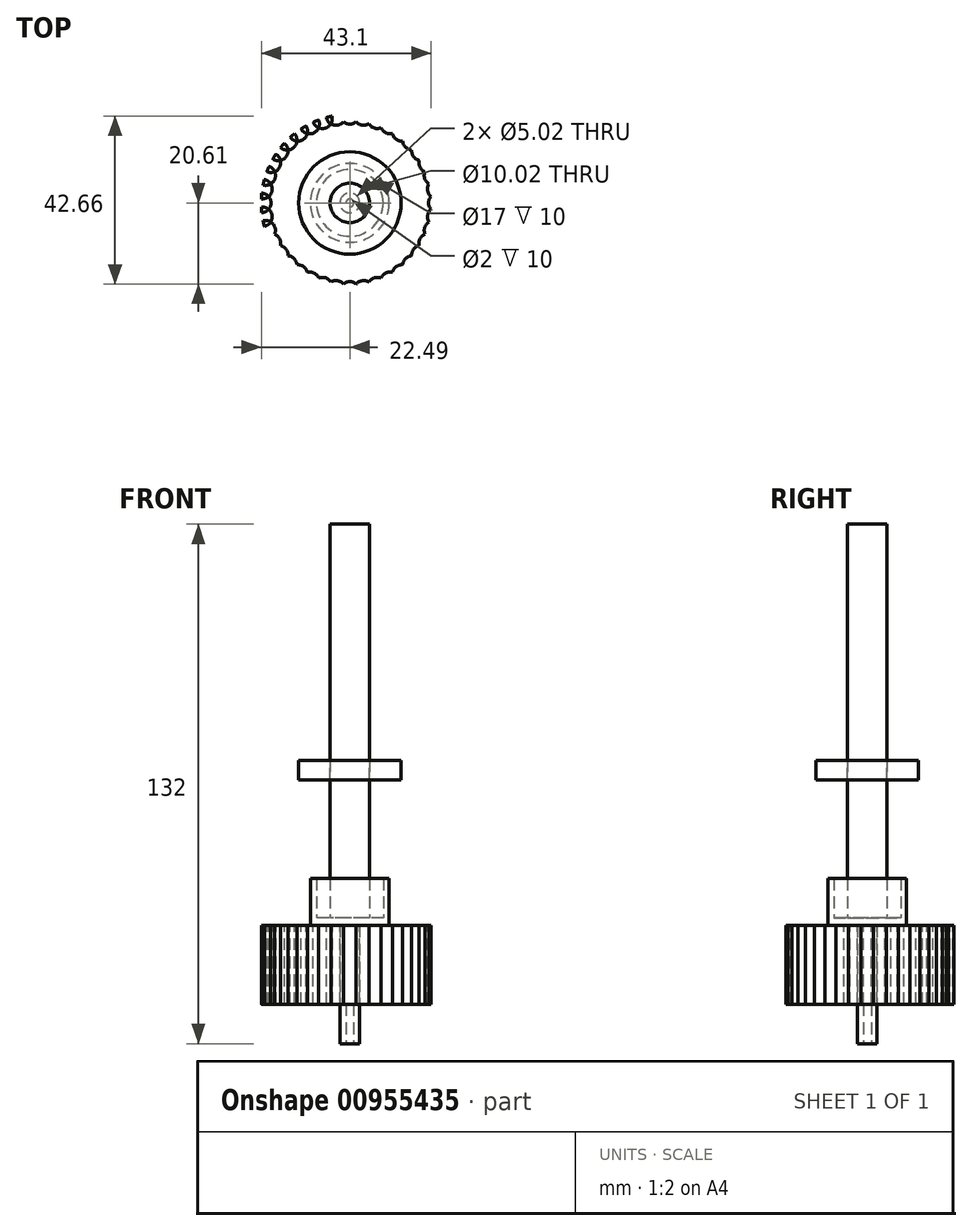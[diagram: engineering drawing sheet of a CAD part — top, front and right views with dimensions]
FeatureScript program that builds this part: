
annotation { "Feature Type Name" : "Feature", "Feature Type Description" : "" }
export const myFeature = defineFeature(function(context is Context, id is Id, definition is map)
    precondition{}
    {
        {
            var Q0;
            Q0=qCreatedBy(makeId("Top.planeOp"),FACE);
            var sketch = newSketch(context, id + "F0", { "sketchPlane" : qUnion([Q0])});
            skCircle(sketch, "E0", {"center": v(0, 0) * mm, "radius": 5 * mm});
            skSolve(sketch);
        }
        {
            var Q0;
            Q0 = qSketchRegion(id + "F0", true);
            extrude(context, id + "F1", {"entities" : qUnion([Q0]), "depth" : 100 * mm, "offsetDistance" : 25 * mm});
        }
        {
            var Q0;
            Q0=qCreatedBy(makeId("Top.planeOp"),FACE);
            var sketch = newSketch(context, id + "F2", { "sketchPlane" : qUnion([Q0])});
            skCircle(sketch, "E1", {"center": v(0, 0) * mm, "radius": 10 * mm});
            skCircle(sketch, "E2", {"center": v(0, 0) * mm, "radius": 5.05 * mm});
            skCircle(sketch, "E3", {"center": v(0, 0) * mm, "radius": 8.5 * mm});
            skSolve(sketch);
        }
        {
            var Q0;
            Q0=makeQuery(id+"F2.imprint","IMPRINT",FACE,{"disambiguationData":[TD([[makeQuery(id+"F2.imprint","IMPRINT",EDGE,{"derivedFrom":sQuery(id+"F2.wireOp",EDGE,"E1")}),1.0]])]});
            extrude(context, id + "F3", {"entities" : qUnion([Q0]), "depth" : 10 * mm, "offsetDistance" : 25 * mm});
        }
        {
            var Q0;
            Q0=qCreatedBy(makeId("Top.planeOp"),FACE);
            var sketch = newSketch(context, id + "F4", { "sketchPlane" : qUnion([Q0])});
            skCircle(sketch, "E4", {"center": v(0, 0) * mm, "radius": 10 * mm});
            skSolve(sketch);
        }
        {
            var Q0;
            Q0 = qSketchRegion(id + "F4", true);
            extrude(context, id + "F5", {"entities" : qUnion([Q0]), "operationType" : NewBodyOperationType.ADD, "oppositeDirection" : true, "depth" : 2 * mm, "offsetDistance" : 25 * mm});
        }
        {
            var Q0;
            Q0=makeQuery(id+"F5.opExtrude","CAP_FACE",FACE,{"disambiguationData":[OSD([sQuery(id+"F4.wireOp",EDGE,"E4")])],"isStart":false});
            var sketch = newSketch(context, id + "F6", { "sketchPlane" : qUnion([Q0])});
            skCircle(sketch, "E5", {"center": v(0, 0) * mm, "radius": 2.5 * mm});
            skSolve(sketch);
        }
        {
            var Q0;
            Q0=makeQuery(id+"F6.imprint","IMPRINT",FACE,{"disambiguationData":[TD([[makeQuery(id+"F6.imprint","IMPRINT",EDGE,{"derivedFrom":sQuery(id+"F6.wireOp",EDGE,"E5")}),1.0]])]});
            extrude(context, id + "F7", {"entities" : qUnion([Q0]), "operationType" : NewBodyOperationType.ADD, "depth" : 30 * mm, "offsetDistance" : 25 * mm});
        }
        {
            var Q0;
            Q0=makeQuery(id+"F7.opExtrude","CAP_FACE",FACE,{"disambiguationData":[OSD([sQuery(id+"F6.wireOp",EDGE,"E5")])],"isStart":false});
            var sketch = newSketch(context, id + "F8", { "sketchPlane" : qUnion([Q0])});
            skCircle(sketch, "E6", {"center": v(0, 0) * mm, "radius": 1 * mm});
            skSolve(sketch);
        }
        {
            var Q0;
            Q0=makeQuery(id+"F8.imprint","IMPRINT",FACE,{"disambiguationData":[TD([[makeQuery(id+"F8.imprint","IMPRINT",EDGE,{"derivedFrom":sQuery(id+"F8.wireOp",EDGE,"E6")}),1.0]])]});
            extrude(context, id + "F9", {"entities" : qUnion([Q0]), "operationType" : NewBodyOperationType.REMOVE, "oppositeDirection" : true, "depth" : 10 * mm, "offsetDistance" : 25 * mm});
        }
        {
            var Q0;
            Q0=qCreatedBy(makeId("Front.planeOp"),FACE);
            var sketch = newSketch(context, id + "F10", { "sketchPlane" : qUnion([Q0])});
            skLineSegment(sketch, "E7.bottom", {"start": v(-2.51, -22) * mm, "end": v(-22.51, -22.01) * mm});
            skLineSegment(sketch, "E7.top", {"start": v(-2.51, -2) * mm, "end": v(-22.51, -2.01) * mm});
            skLineSegment(sketch, "E7.left", {"start": v(-2.51, -22) * mm, "end": v(-2.51, -2) * mm});
            skLineSegment(sketch, "E7.right", {"start": v(-22.51, -22.01) * mm, "end": v(-22.51, -2.01) * mm});
            skSolve(sketch);
        }
        {
            var Q0;
            Q0 = qSketchRegion(id + "F10", true);
            var Q1;
            Q1=makeQuery(id+"F7.opExtrude","SWEPT_FACE",FACE,{"disambiguationData":[OSD([sQuery(id+"F6.wireOp",EDGE,"E5")])]});
            revolve(context, id + "F11", {"surfaceOperationType" : NewSurfaceOperationType.NEW, "entities" : qUnion([Q0]), "axis" : qUnion([Q1]), "revolveType" : RevolveType.FULL});
        }
        {
            var Q0;
            Q0=makeQuery(id+"F11.opRevolve","SWEPT_FACE",FACE,{"disambiguationData":[OSD([sQuery(id+"F10.wireOp",EDGE,"E7.top")])]});
            var sketch = newSketch(context, id + "F12", { "sketchPlane" : qUnion([Q0])});
            skCircle(sketch, "E8", {"center": v(0, 22.51) * mm, "radius": 2.5 * mm});
            skCircle(sketch, "E9.1.0", {"center": v(-3.52, 22.23) * mm, "radius": 2.5 * mm});
            skCircle(sketch, "E9.2.0", {"center": v(-6.96, 21.4) * mm, "radius": 2.5 * mm});
            skCircle(sketch, "E9.3.0", {"center": v(-10.22, 20.06) * mm, "radius": 2.5 * mm});
            skCircle(sketch, "E9.4.0", {"center": v(-13.23, 18.21) * mm, "radius": 2.5 * mm});
            skCircle(sketch, "E9.5.0", {"center": v(-15.92, 15.92) * mm, "radius": 2.5 * mm});
            skCircle(sketch, "E9.6.0", {"center": v(-18.21, 13.23) * mm, "radius": 2.5 * mm});
            skCircle(sketch, "E9.7.0", {"center": v(-20.06, 10.22) * mm, "radius": 2.5 * mm});
            skCircle(sketch, "E9.8.0", {"center": v(-21.4, 6.96) * mm, "radius": 2.5 * mm});
            skCircle(sketch, "E9.9.0", {"center": v(-22.23, 3.52) * mm, "radius": 2.5 * mm});
            skCircle(sketch, "E9.10.0", {"center": v(-22.51, 0) * mm, "radius": 2.5 * mm});
            skCircle(sketch, "E9.11.0", {"center": v(-22.23, -3.52) * mm, "radius": 2.5 * mm});
            skPoint(sketch, "E9.center", {"position": v(0, 0) * mm});
            skCircle(sketch, "E10.1.12.0", {"center": v(-21.4, -6.96) * mm, "radius": 2.5 * mm});
            skCircle(sketch, "E10.1.13.0", {"center": v(-20.06, -10.22) * mm, "radius": 2.5 * mm});
            skCircle(sketch, "E10.1.14.0", {"center": v(-18.21, -13.23) * mm, "radius": 2.5 * mm});
            skCircle(sketch, "E10.1.15.0", {"center": v(-15.92, -15.92) * mm, "radius": 2.5 * mm});
            skCircle(sketch, "E10.1.16.0", {"center": v(-13.23, -18.21) * mm, "radius": 2.5 * mm});
            skCircle(sketch, "E10.1.17.0", {"center": v(-10.22, -20.06) * mm, "radius": 2.5 * mm});
            skCircle(sketch, "E10.1.18.0", {"center": v(-6.96, -21.4) * mm, "radius": 2.5 * mm});
            skCircle(sketch, "E10.1.19.0", {"center": v(-3.52, -22.23) * mm, "radius": 2.5 * mm});
            skCircle(sketch, "E10.1.20.0", {"center": v(0, -22.51) * mm, "radius": 2.5 * mm});
            skCircle(sketch, "E10.1.21.0", {"center": v(3.52, -22.23) * mm, "radius": 2.5 * mm});
            skCircle(sketch, "E10.1.22.0", {"center": v(6.96, -21.4) * mm, "radius": 2.5 * mm});
            skCircle(sketch, "E10.1.23.0", {"center": v(10.22, -20.06) * mm, "radius": 2.5 * mm});
            skCircle(sketch, "E10.1.24.0", {"center": v(13.23, -18.21) * mm, "radius": 2.5 * mm});
            skCircle(sketch, "E10.1.25.0", {"center": v(15.92, -15.92) * mm, "radius": 2.5 * mm});
            skCircle(sketch, "E10.1.26.0", {"center": v(18.21, -13.23) * mm, "radius": 2.5 * mm});
            skCircle(sketch, "E10.1.27.0", {"center": v(20.06, -10.22) * mm, "radius": 2.5 * mm});
            skCircle(sketch, "E10.1.28.0", {"center": v(21.4, -6.96) * mm, "radius": 2.5 * mm});
            skCircle(sketch, "E10.1.29.0", {"center": v(22.23, -3.52) * mm, "radius": 2.5 * mm});
            skCircle(sketch, "E10.1.30.0", {"center": v(22.51, 0) * mm, "radius": 2.5 * mm});
            skCircle(sketch, "E10.1.31.0", {"center": v(22.23, 3.52) * mm, "radius": 2.5 * mm});
            skCircle(sketch, "E10.1.32.0", {"center": v(21.4, 6.96) * mm, "radius": 2.5 * mm});
            skCircle(sketch, "E11.1.33.0", {"center": v(20.06, 10.22) * mm, "radius": 2.5 * mm});
            skCircle(sketch, "E11.1.34.0", {"center": v(18.21, 13.23) * mm, "radius": 2.5 * mm});
            skCircle(sketch, "E12.1.35.0", {"center": v(15.92, 15.92) * mm, "radius": 2.5 * mm});
            skCircle(sketch, "E12.1.36.0", {"center": v(13.23, 18.21) * mm, "radius": 2.5 * mm});
            skCircle(sketch, "E12.1.37.0", {"center": v(10.22, 20.06) * mm, "radius": 2.5 * mm});
            skCircle(sketch, "E12.1.38.0", {"center": v(6.96, 21.4) * mm, "radius": 2.5 * mm});
            skCircle(sketch, "E12.1.39.0", {"center": v(3.52, 22.23) * mm, "radius": 2.5 * mm});
            skSolve(sketch);
        }
        {
            var Q0;
            {var subQ0=sQuery(id+"F12.wireOp",EDGE,"E9.1.0");var subQ1=makeQuery(id+"F11.opRevolve","SWEPT_EDGE",EDGE,{"disambiguationData":[OSD([sQuery(id+"F10.wireOp",EDGE,"E7.top"),sQuery(id+"F10.wireOp",EDGE,"E7.right")])]});var subQ2=makeQuery(id+"F12.imprint","INTERSECT",VERTEX,{"disambiguationData":[OD(0.0)],"derivedFrom":[subQ1,subQ0]});Q0=makeQuery(id+"F12.imprint","IMPRINT",FACE,{"disambiguationData":[TD([[makeQuery(id+"F12.imprint","IMPRINT",EDGE,{"disambiguationData":[TD([[subQ2,-1.0]])],"derivedFrom":subQ0}),1.0]])]});}
            var Q1;
            {var subQ0=sQuery(id+"F12.wireOp",EDGE,"E8");var subQ1=makeQuery(id+"F11.opRevolve","SWEPT_EDGE",EDGE,{"disambiguationData":[OSD([sQuery(id+"F10.wireOp",EDGE,"E7.top"),sQuery(id+"F10.wireOp",EDGE,"E7.right")])]});var subQ2=makeQuery(id+"F12.imprint","INTERSECT",VERTEX,{"disambiguationData":[OD(0.0)],"derivedFrom":[subQ1,subQ0]});Q1=makeQuery(id+"F12.imprint","IMPRINT",FACE,{"disambiguationData":[TD([[makeQuery(id+"F12.imprint","IMPRINT",EDGE,{"disambiguationData":[TD([[subQ2,-1.0]])],"derivedFrom":subQ0}),1.0]])]});}
            var Q2;
            {var subQ0=sQuery(id+"F12.wireOp",EDGE,"E9.11.0");var subQ1=makeQuery(id+"F11.opRevolve","SWEPT_EDGE",EDGE,{"disambiguationData":[OSD([sQuery(id+"F10.wireOp",EDGE,"E7.top"),sQuery(id+"F10.wireOp",EDGE,"E7.right")])]});var subQ2=makeQuery(id+"F12.imprint","INTERSECT",VERTEX,{"disambiguationData":[OD(0.0)],"derivedFrom":[subQ1,subQ0]});Q2=makeQuery(id+"F12.imprint","IMPRINT",FACE,{"disambiguationData":[TD([[makeQuery(id+"F12.imprint","IMPRINT",EDGE,{"disambiguationData":[TD([[subQ2,-1.0]])],"derivedFrom":subQ0}),1.0]])]});}
            var Q3;
            {var subQ0=sQuery(id+"F12.wireOp",EDGE,"E9.10.0");var subQ1=makeQuery(id+"F11.opRevolve","SWEPT_EDGE",EDGE,{"disambiguationData":[OSD([sQuery(id+"F10.wireOp",EDGE,"E7.top"),sQuery(id+"F10.wireOp",EDGE,"E7.right")])]});var subQ2=makeQuery(id+"F12.imprint","INTERSECT",VERTEX,{"disambiguationData":[OD(0.0)],"derivedFrom":[subQ1,subQ0]});Q3=makeQuery(id+"F12.imprint","IMPRINT",FACE,{"disambiguationData":[TD([[makeQuery(id+"F12.imprint","IMPRINT",EDGE,{"disambiguationData":[TD([[subQ2,-1.0]])],"derivedFrom":subQ0}),1.0]])]});}
            var Q4;
            {var subQ0=sQuery(id+"F12.wireOp",EDGE,"E9.3.0");var subQ1=makeQuery(id+"F11.opRevolve","SWEPT_EDGE",EDGE,{"disambiguationData":[OSD([sQuery(id+"F10.wireOp",EDGE,"E7.top"),sQuery(id+"F10.wireOp",EDGE,"E7.right")])]});var subQ2=makeQuery(id+"F12.imprint","INTERSECT",VERTEX,{"disambiguationData":[OD(0.0)],"derivedFrom":[subQ1,subQ0]});Q4=makeQuery(id+"F12.imprint","IMPRINT",FACE,{"disambiguationData":[TD([[makeQuery(id+"F12.imprint","IMPRINT",EDGE,{"disambiguationData":[TD([[subQ2,-1.0]])],"derivedFrom":subQ0}),1.0]])]});}
            var Q5;
            {var subQ0=sQuery(id+"F12.wireOp",EDGE,"E9.2.0");var subQ1=makeQuery(id+"F11.opRevolve","SWEPT_EDGE",EDGE,{"disambiguationData":[OSD([sQuery(id+"F10.wireOp",EDGE,"E7.top"),sQuery(id+"F10.wireOp",EDGE,"E7.right")])]});var subQ2=makeQuery(id+"F12.imprint","INTERSECT",VERTEX,{"disambiguationData":[OD(0.0)],"derivedFrom":[subQ1,subQ0]});Q5=makeQuery(id+"F12.imprint","IMPRINT",FACE,{"disambiguationData":[TD([[makeQuery(id+"F12.imprint","IMPRINT",EDGE,{"disambiguationData":[TD([[subQ2,-1.0]])],"derivedFrom":subQ0}),1.0]])]});}
            var Q6;
            {var subQ0=sQuery(id+"F12.wireOp",EDGE,"E12.1.39.0");var subQ1=makeQuery(id+"F11.opRevolve","SWEPT_EDGE",EDGE,{"disambiguationData":[OSD([sQuery(id+"F10.wireOp",EDGE,"E7.top"),sQuery(id+"F10.wireOp",EDGE,"E7.right")])]});var subQ2=makeQuery(id+"F12.imprint","INTERSECT",VERTEX,{"disambiguationData":[OD(0.0)],"derivedFrom":[subQ1,subQ0]});Q6=makeQuery(id+"F12.imprint","IMPRINT",FACE,{"disambiguationData":[TD([[makeQuery(id+"F12.imprint","IMPRINT",EDGE,{"disambiguationData":[TD([[subQ2,-1.0]])],"derivedFrom":subQ0}),1.0]])]});}
            var Q7;
            {var subQ0=sQuery(id+"F12.wireOp",EDGE,"E12.1.38.0");var subQ1=makeQuery(id+"F11.opRevolve","SWEPT_EDGE",EDGE,{"disambiguationData":[OSD([sQuery(id+"F10.wireOp",EDGE,"E7.top"),sQuery(id+"F10.wireOp",EDGE,"E7.right")])]});var subQ2=makeQuery(id+"F12.imprint","INTERSECT",VERTEX,{"disambiguationData":[OD(0.0)],"derivedFrom":[subQ1,subQ0]});Q7=makeQuery(id+"F12.imprint","IMPRINT",FACE,{"disambiguationData":[TD([[makeQuery(id+"F12.imprint","IMPRINT",EDGE,{"disambiguationData":[TD([[subQ2,-1.0]])],"derivedFrom":subQ0}),1.0]])]});}
            var Q8;
            {var subQ0=sQuery(id+"F12.wireOp",EDGE,"E12.1.37.0");var subQ1=makeQuery(id+"F11.opRevolve","SWEPT_EDGE",EDGE,{"disambiguationData":[OSD([sQuery(id+"F10.wireOp",EDGE,"E7.top"),sQuery(id+"F10.wireOp",EDGE,"E7.right")])]});var subQ2=makeQuery(id+"F12.imprint","INTERSECT",VERTEX,{"disambiguationData":[OD(0.0)],"derivedFrom":[subQ1,subQ0]});Q8=makeQuery(id+"F12.imprint","IMPRINT",FACE,{"disambiguationData":[TD([[makeQuery(id+"F12.imprint","IMPRINT",EDGE,{"disambiguationData":[TD([[subQ2,-1.0]])],"derivedFrom":subQ0}),1.0]])]});}
            var Q9;
            {var subQ0=sQuery(id+"F12.wireOp",EDGE,"E12.1.36.0");var subQ1=makeQuery(id+"F11.opRevolve","SWEPT_EDGE",EDGE,{"disambiguationData":[OSD([sQuery(id+"F10.wireOp",EDGE,"E7.top"),sQuery(id+"F10.wireOp",EDGE,"E7.right")])]});var subQ2=makeQuery(id+"F12.imprint","INTERSECT",VERTEX,{"disambiguationData":[OD(0.0)],"derivedFrom":[subQ1,subQ0]});Q9=makeQuery(id+"F12.imprint","IMPRINT",FACE,{"disambiguationData":[TD([[makeQuery(id+"F12.imprint","IMPRINT",EDGE,{"disambiguationData":[TD([[subQ2,-1.0]])],"derivedFrom":subQ0}),1.0]])]});}
            var Q10;
            {var subQ0=sQuery(id+"F12.wireOp",EDGE,"E12.1.35.0");var subQ1=makeQuery(id+"F11.opRevolve","SWEPT_EDGE",EDGE,{"disambiguationData":[OSD([sQuery(id+"F10.wireOp",EDGE,"E7.top"),sQuery(id+"F10.wireOp",EDGE,"E7.right")])]});var subQ2=makeQuery(id+"F12.imprint","INTERSECT",VERTEX,{"disambiguationData":[OD(0.0)],"derivedFrom":[subQ1,subQ0]});Q10=makeQuery(id+"F12.imprint","IMPRINT",FACE,{"disambiguationData":[TD([[makeQuery(id+"F12.imprint","IMPRINT",EDGE,{"disambiguationData":[TD([[subQ2,-1.0]])],"derivedFrom":subQ0}),1.0]])]});}
            var Q11;
            {var subQ0=sQuery(id+"F12.wireOp",EDGE,"E11.1.34.0");var subQ1=makeQuery(id+"F11.opRevolve","SWEPT_EDGE",EDGE,{"disambiguationData":[OSD([sQuery(id+"F10.wireOp",EDGE,"E7.top"),sQuery(id+"F10.wireOp",EDGE,"E7.right")])]});var subQ2=makeQuery(id+"F12.imprint","INTERSECT",VERTEX,{"disambiguationData":[OD(0.0)],"derivedFrom":[subQ1,subQ0]});Q11=makeQuery(id+"F12.imprint","IMPRINT",FACE,{"disambiguationData":[TD([[makeQuery(id+"F12.imprint","IMPRINT",EDGE,{"disambiguationData":[TD([[subQ2,-1.0]])],"derivedFrom":subQ0}),1.0]])]});}
            var Q12;
            {var subQ0=sQuery(id+"F12.wireOp",EDGE,"E11.1.33.0");var subQ1=makeQuery(id+"F11.opRevolve","SWEPT_EDGE",EDGE,{"disambiguationData":[OSD([sQuery(id+"F10.wireOp",EDGE,"E7.top"),sQuery(id+"F10.wireOp",EDGE,"E7.right")])]});var subQ2=makeQuery(id+"F12.imprint","INTERSECT",VERTEX,{"disambiguationData":[OD(0.0)],"derivedFrom":[subQ1,subQ0]});Q12=makeQuery(id+"F12.imprint","IMPRINT",FACE,{"disambiguationData":[TD([[makeQuery(id+"F12.imprint","IMPRINT",EDGE,{"disambiguationData":[TD([[subQ2,-1.0]])],"derivedFrom":subQ0}),1.0]])]});}
            var Q13;
            {var subQ0=sQuery(id+"F12.wireOp",EDGE,"E10.1.19.0");var subQ1=makeQuery(id+"F11.opRevolve","SWEPT_EDGE",EDGE,{"disambiguationData":[OSD([sQuery(id+"F10.wireOp",EDGE,"E7.top"),sQuery(id+"F10.wireOp",EDGE,"E7.right")])]});var subQ2=makeQuery(id+"F12.imprint","INTERSECT",VERTEX,{"disambiguationData":[OD(0.0)],"derivedFrom":[subQ1,subQ0]});Q13=makeQuery(id+"F12.imprint","IMPRINT",FACE,{"disambiguationData":[TD([[makeQuery(id+"F12.imprint","IMPRINT",EDGE,{"disambiguationData":[TD([[subQ2,1.0]])],"derivedFrom":subQ0}),1.0]])]});}
            var Q14;
            {var subQ0=sQuery(id+"F12.wireOp",EDGE,"E10.1.18.0");var subQ1=makeQuery(id+"F11.opRevolve","SWEPT_EDGE",EDGE,{"disambiguationData":[OSD([sQuery(id+"F10.wireOp",EDGE,"E7.top"),sQuery(id+"F10.wireOp",EDGE,"E7.right")])]});var subQ2=makeQuery(id+"F12.imprint","INTERSECT",VERTEX,{"disambiguationData":[OD(0.0)],"derivedFrom":[subQ1,subQ0]});Q14=makeQuery(id+"F12.imprint","IMPRINT",FACE,{"disambiguationData":[TD([[makeQuery(id+"F12.imprint","IMPRINT",EDGE,{"disambiguationData":[TD([[subQ2,1.0]])],"derivedFrom":subQ0}),1.0]])]});}
            var Q15;
            {var subQ0=sQuery(id+"F12.wireOp",EDGE,"E10.1.17.0");var subQ1=makeQuery(id+"F11.opRevolve","SWEPT_EDGE",EDGE,{"disambiguationData":[OSD([sQuery(id+"F10.wireOp",EDGE,"E7.top"),sQuery(id+"F10.wireOp",EDGE,"E7.right")])]});var subQ2=makeQuery(id+"F12.imprint","INTERSECT",VERTEX,{"disambiguationData":[OD(0.0)],"derivedFrom":[subQ1,subQ0]});Q15=makeQuery(id+"F12.imprint","IMPRINT",FACE,{"disambiguationData":[TD([[makeQuery(id+"F12.imprint","IMPRINT",EDGE,{"disambiguationData":[TD([[subQ2,1.0]])],"derivedFrom":subQ0}),1.0]])]});}
            var Q16;
            {var subQ0=sQuery(id+"F12.wireOp",EDGE,"E10.1.16.0");var subQ1=makeQuery(id+"F11.opRevolve","SWEPT_EDGE",EDGE,{"disambiguationData":[OSD([sQuery(id+"F10.wireOp",EDGE,"E7.top"),sQuery(id+"F10.wireOp",EDGE,"E7.right")])]});var subQ2=makeQuery(id+"F12.imprint","INTERSECT",VERTEX,{"disambiguationData":[OD(0.0)],"derivedFrom":[subQ1,subQ0]});Q16=makeQuery(id+"F12.imprint","IMPRINT",FACE,{"disambiguationData":[TD([[makeQuery(id+"F12.imprint","IMPRINT",EDGE,{"disambiguationData":[TD([[subQ2,1.0]])],"derivedFrom":subQ0}),1.0]])]});}
            var Q17;
            {var subQ0=sQuery(id+"F12.wireOp",EDGE,"E10.1.15.0");var subQ1=makeQuery(id+"F11.opRevolve","SWEPT_EDGE",EDGE,{"disambiguationData":[OSD([sQuery(id+"F10.wireOp",EDGE,"E7.top"),sQuery(id+"F10.wireOp",EDGE,"E7.right")])]});var subQ2=makeQuery(id+"F12.imprint","INTERSECT",VERTEX,{"disambiguationData":[OD(0.0)],"derivedFrom":[subQ1,subQ0]});Q17=makeQuery(id+"F12.imprint","IMPRINT",FACE,{"disambiguationData":[TD([[makeQuery(id+"F12.imprint","IMPRINT",EDGE,{"disambiguationData":[TD([[subQ2,1.0]])],"derivedFrom":subQ0}),1.0]])]});}
            var Q18;
            {var subQ0=sQuery(id+"F12.wireOp",EDGE,"E10.1.14.0");var subQ1=makeQuery(id+"F11.opRevolve","SWEPT_EDGE",EDGE,{"disambiguationData":[OSD([sQuery(id+"F10.wireOp",EDGE,"E7.top"),sQuery(id+"F10.wireOp",EDGE,"E7.right")])]});var subQ2=makeQuery(id+"F12.imprint","INTERSECT",VERTEX,{"disambiguationData":[OD(0.0)],"derivedFrom":[subQ1,subQ0]});Q18=makeQuery(id+"F12.imprint","IMPRINT",FACE,{"disambiguationData":[TD([[makeQuery(id+"F12.imprint","IMPRINT",EDGE,{"disambiguationData":[TD([[subQ2,1.0]])],"derivedFrom":subQ0}),1.0]])]});}
            var Q19;
            {var subQ0=sQuery(id+"F12.wireOp",EDGE,"E10.1.13.0");var subQ1=makeQuery(id+"F11.opRevolve","SWEPT_EDGE",EDGE,{"disambiguationData":[OSD([sQuery(id+"F10.wireOp",EDGE,"E7.top"),sQuery(id+"F10.wireOp",EDGE,"E7.right")])]});var subQ2=makeQuery(id+"F12.imprint","INTERSECT",VERTEX,{"disambiguationData":[OD(0.0)],"derivedFrom":[subQ1,subQ0]});Q19=makeQuery(id+"F12.imprint","IMPRINT",FACE,{"disambiguationData":[TD([[makeQuery(id+"F12.imprint","IMPRINT",EDGE,{"disambiguationData":[TD([[subQ2,1.0]])],"derivedFrom":subQ0}),1.0]])]});}
            var Q20;
            {var subQ0=sQuery(id+"F12.wireOp",EDGE,"E10.1.12.0");var subQ1=makeQuery(id+"F11.opRevolve","SWEPT_EDGE",EDGE,{"disambiguationData":[OSD([sQuery(id+"F10.wireOp",EDGE,"E7.top"),sQuery(id+"F10.wireOp",EDGE,"E7.right")])]});var subQ2=makeQuery(id+"F12.imprint","INTERSECT",VERTEX,{"disambiguationData":[OD(0.0)],"derivedFrom":[subQ1,subQ0]});Q20=makeQuery(id+"F12.imprint","IMPRINT",FACE,{"disambiguationData":[TD([[makeQuery(id+"F12.imprint","IMPRINT",EDGE,{"disambiguationData":[TD([[subQ2,-1.0]])],"derivedFrom":subQ0}),1.0]])]});}
            var Q21;
            {var subQ0=sQuery(id+"F12.wireOp",EDGE,"E10.1.13.0");var subQ1=makeQuery(id+"F11.opRevolve","SWEPT_EDGE",EDGE,{"disambiguationData":[OSD([sQuery(id+"F10.wireOp",EDGE,"E7.top"),sQuery(id+"F10.wireOp",EDGE,"E7.right")])]});var subQ2=makeQuery(id+"F12.imprint","INTERSECT",VERTEX,{"disambiguationData":[OD(0.0)],"derivedFrom":[subQ1,subQ0]});Q21=makeQuery(id+"F12.imprint","IMPRINT",FACE,{"disambiguationData":[TD([[makeQuery(id+"F12.imprint","IMPRINT",EDGE,{"disambiguationData":[TD([[subQ2,-1.0]])],"derivedFrom":subQ0}),1.0]])]});}
            var Q22;
            {var subQ0=sQuery(id+"F12.wireOp",EDGE,"E9.9.0");var subQ1=makeQuery(id+"F11.opRevolve","SWEPT_EDGE",EDGE,{"disambiguationData":[OSD([sQuery(id+"F10.wireOp",EDGE,"E7.top"),sQuery(id+"F10.wireOp",EDGE,"E7.right")])]});var subQ2=makeQuery(id+"F12.imprint","INTERSECT",VERTEX,{"disambiguationData":[OD(0.0)],"derivedFrom":[subQ1,subQ0]});Q22=makeQuery(id+"F12.imprint","IMPRINT",FACE,{"disambiguationData":[TD([[makeQuery(id+"F12.imprint","IMPRINT",EDGE,{"disambiguationData":[TD([[subQ2,-1.0]])],"derivedFrom":subQ0}),1.0]])]});}
            var Q23;
            {var subQ0=sQuery(id+"F12.wireOp",EDGE,"E9.8.0");var subQ1=makeQuery(id+"F11.opRevolve","SWEPT_EDGE",EDGE,{"disambiguationData":[OSD([sQuery(id+"F10.wireOp",EDGE,"E7.top"),sQuery(id+"F10.wireOp",EDGE,"E7.right")])]});var subQ2=makeQuery(id+"F12.imprint","INTERSECT",VERTEX,{"disambiguationData":[OD(0.0)],"derivedFrom":[subQ1,subQ0]});Q23=makeQuery(id+"F12.imprint","IMPRINT",FACE,{"disambiguationData":[TD([[makeQuery(id+"F12.imprint","IMPRINT",EDGE,{"disambiguationData":[TD([[subQ2,-1.0]])],"derivedFrom":subQ0}),1.0]])]});}
            var Q24;
            {var subQ0=sQuery(id+"F12.wireOp",EDGE,"E9.7.0");var subQ1=makeQuery(id+"F11.opRevolve","SWEPT_EDGE",EDGE,{"disambiguationData":[OSD([sQuery(id+"F10.wireOp",EDGE,"E7.top"),sQuery(id+"F10.wireOp",EDGE,"E7.right")])]});var subQ2=makeQuery(id+"F12.imprint","INTERSECT",VERTEX,{"disambiguationData":[OD(0.0)],"derivedFrom":[subQ1,subQ0]});Q24=makeQuery(id+"F12.imprint","IMPRINT",FACE,{"disambiguationData":[TD([[makeQuery(id+"F12.imprint","IMPRINT",EDGE,{"disambiguationData":[TD([[subQ2,-1.0]])],"derivedFrom":subQ0}),1.0]])]});}
            var Q25;
            {var subQ0=sQuery(id+"F12.wireOp",EDGE,"E9.6.0");var subQ1=makeQuery(id+"F11.opRevolve","SWEPT_EDGE",EDGE,{"disambiguationData":[OSD([sQuery(id+"F10.wireOp",EDGE,"E7.top"),sQuery(id+"F10.wireOp",EDGE,"E7.right")])]});var subQ2=makeQuery(id+"F12.imprint","INTERSECT",VERTEX,{"disambiguationData":[OD(0.0)],"derivedFrom":[subQ1,subQ0]});Q25=makeQuery(id+"F12.imprint","IMPRINT",FACE,{"disambiguationData":[TD([[makeQuery(id+"F12.imprint","IMPRINT",EDGE,{"disambiguationData":[TD([[subQ2,-1.0]])],"derivedFrom":subQ0}),1.0]])]});}
            var Q26;
            {var subQ0=sQuery(id+"F12.wireOp",EDGE,"E9.5.0");var subQ1=makeQuery(id+"F11.opRevolve","SWEPT_EDGE",EDGE,{"disambiguationData":[OSD([sQuery(id+"F10.wireOp",EDGE,"E7.top"),sQuery(id+"F10.wireOp",EDGE,"E7.right")])]});var subQ2=makeQuery(id+"F12.imprint","INTERSECT",VERTEX,{"disambiguationData":[OD(0.0)],"derivedFrom":[subQ1,subQ0]});Q26=makeQuery(id+"F12.imprint","IMPRINT",FACE,{"disambiguationData":[TD([[makeQuery(id+"F12.imprint","IMPRINT",EDGE,{"disambiguationData":[TD([[subQ2,-1.0]])],"derivedFrom":subQ0}),1.0]])]});}
            var Q27;
            {var subQ0=sQuery(id+"F12.wireOp",EDGE,"E9.4.0");var subQ1=makeQuery(id+"F11.opRevolve","SWEPT_EDGE",EDGE,{"disambiguationData":[OSD([sQuery(id+"F10.wireOp",EDGE,"E7.top"),sQuery(id+"F10.wireOp",EDGE,"E7.right")])]});var subQ2=makeQuery(id+"F12.imprint","INTERSECT",VERTEX,{"disambiguationData":[OD(0.0)],"derivedFrom":[subQ1,subQ0]});Q27=makeQuery(id+"F12.imprint","IMPRINT",FACE,{"disambiguationData":[TD([[makeQuery(id+"F12.imprint","IMPRINT",EDGE,{"disambiguationData":[TD([[subQ2,-1.0]])],"derivedFrom":subQ0}),1.0]])]});}
            var Q28;
            {var subQ0=sQuery(id+"F12.wireOp",EDGE,"E11.1.34.0");var subQ1=sQuery(id+"F12.wireOp",EDGE,"E11.1.33.0");var subQ2=makeQuery(id+"F12.imprint","INTERSECT",VERTEX,{"disambiguationData":[OD(1.0)],"derivedFrom":[subQ1,subQ0]});Q28=makeQuery(id+"F12.imprint","IMPRINT",FACE,{"disambiguationData":[TD([[makeQuery(id+"F12.imprint","IMPRINT",EDGE,{"disambiguationData":[TD([[subQ2,1.0]])],"derivedFrom":subQ0}),1.0]])]});}
            var Q29;
            {var subQ0=sQuery(id+"F12.wireOp",EDGE,"E12.1.35.0");var subQ1=sQuery(id+"F12.wireOp",EDGE,"E11.1.34.0");var subQ2=makeQuery(id+"F12.imprint","INTERSECT",VERTEX,{"disambiguationData":[OD(1.0)],"derivedFrom":[subQ1,subQ0]});Q29=makeQuery(id+"F12.imprint","IMPRINT",FACE,{"disambiguationData":[TD([[makeQuery(id+"F12.imprint","IMPRINT",EDGE,{"disambiguationData":[TD([[subQ2,1.0]])],"derivedFrom":subQ0}),1.0]])]});}
            var Q30;
            {var subQ0=sQuery(id+"F12.wireOp",EDGE,"E12.1.36.0");var subQ1=sQuery(id+"F12.wireOp",EDGE,"E12.1.35.0");var subQ2=makeQuery(id+"F12.imprint","INTERSECT",VERTEX,{"disambiguationData":[OD(1.0)],"derivedFrom":[subQ1,subQ0]});Q30=makeQuery(id+"F12.imprint","IMPRINT",FACE,{"disambiguationData":[TD([[makeQuery(id+"F12.imprint","IMPRINT",EDGE,{"disambiguationData":[TD([[subQ2,1.0]])],"derivedFrom":subQ0}),1.0]])]});}
            var Q31;
            {var subQ0=sQuery(id+"F12.wireOp",EDGE,"E12.1.37.0");var subQ1=sQuery(id+"F12.wireOp",EDGE,"E12.1.36.0");var subQ2=makeQuery(id+"F12.imprint","INTERSECT",VERTEX,{"disambiguationData":[OD(1.0)],"derivedFrom":[subQ1,subQ0]});Q31=makeQuery(id+"F12.imprint","IMPRINT",FACE,{"disambiguationData":[TD([[makeQuery(id+"F12.imprint","IMPRINT",EDGE,{"disambiguationData":[TD([[subQ2,1.0]])],"derivedFrom":subQ0}),1.0]])]});}
            var Q32;
            {var subQ0=sQuery(id+"F12.wireOp",EDGE,"E12.1.38.0");var subQ1=sQuery(id+"F12.wireOp",EDGE,"E12.1.37.0");var subQ2=makeQuery(id+"F12.imprint","INTERSECT",VERTEX,{"disambiguationData":[OD(1.0)],"derivedFrom":[subQ1,subQ0]});Q32=makeQuery(id+"F12.imprint","IMPRINT",FACE,{"disambiguationData":[TD([[makeQuery(id+"F12.imprint","IMPRINT",EDGE,{"disambiguationData":[TD([[subQ2,1.0]])],"derivedFrom":subQ0}),1.0]])]});}
            var Q33;
            {var subQ0=sQuery(id+"F12.wireOp",EDGE,"E12.1.39.0");var subQ1=sQuery(id+"F12.wireOp",EDGE,"E8");var subQ2=makeQuery(id+"F12.imprint","INTERSECT",VERTEX,{"disambiguationData":[OD(1.0)],"derivedFrom":[subQ1,subQ0]});Q33=makeQuery(id+"F12.imprint","IMPRINT",FACE,{"disambiguationData":[TD([[makeQuery(id+"F12.imprint","IMPRINT",EDGE,{"disambiguationData":[TD([[subQ2,-1.0]])],"derivedFrom":subQ0}),1.0]])]});}
            var Q34;
            {var subQ0=sQuery(id+"F12.wireOp",EDGE,"E9.1.0");var subQ1=sQuery(id+"F12.wireOp",EDGE,"E8");var subQ2=makeQuery(id+"F12.imprint","INTERSECT",VERTEX,{"disambiguationData":[OD(1.0)],"derivedFrom":[subQ1,subQ0]});Q34=makeQuery(id+"F12.imprint","IMPRINT",FACE,{"disambiguationData":[TD([[makeQuery(id+"F12.imprint","IMPRINT",EDGE,{"disambiguationData":[TD([[subQ2,-1.0]])],"derivedFrom":subQ1}),1.0]])]});}
            var Q35;
            {var subQ0=sQuery(id+"F12.wireOp",EDGE,"E9.1.0");var subQ1=sQuery(id+"F12.wireOp",EDGE,"E8");var subQ2=makeQuery(id+"F12.imprint","INTERSECT",VERTEX,{"disambiguationData":[OD(1.0)],"derivedFrom":[subQ1,subQ0]});Q35=makeQuery(id+"F12.imprint","IMPRINT",FACE,{"disambiguationData":[TD([[makeQuery(id+"F12.imprint","IMPRINT",EDGE,{"disambiguationData":[TD([[subQ2,1.0]])],"derivedFrom":subQ0}),1.0]])]});}
            var Q36;
            {var subQ0=sQuery(id+"F12.wireOp",EDGE,"E9.2.0");var subQ1=sQuery(id+"F12.wireOp",EDGE,"E9.1.0");var subQ2=makeQuery(id+"F12.imprint","INTERSECT",VERTEX,{"disambiguationData":[OD(1.0)],"derivedFrom":[subQ1,subQ0]});Q36=makeQuery(id+"F12.imprint","IMPRINT",FACE,{"disambiguationData":[TD([[makeQuery(id+"F12.imprint","IMPRINT",EDGE,{"disambiguationData":[TD([[subQ2,1.0]])],"derivedFrom":subQ0}),1.0]])]});}
            var Q37;
            {var subQ0=sQuery(id+"F12.wireOp",EDGE,"E9.3.0");var subQ1=sQuery(id+"F12.wireOp",EDGE,"E9.2.0");var subQ2=makeQuery(id+"F12.imprint","INTERSECT",VERTEX,{"disambiguationData":[OD(1.0)],"derivedFrom":[subQ1,subQ0]});Q37=makeQuery(id+"F12.imprint","IMPRINT",FACE,{"disambiguationData":[TD([[makeQuery(id+"F12.imprint","IMPRINT",EDGE,{"disambiguationData":[TD([[subQ2,1.0]])],"derivedFrom":subQ0}),1.0]])]});}
            var Q38;
            {var subQ0=sQuery(id+"F12.wireOp",EDGE,"E9.4.0");var subQ1=sQuery(id+"F12.wireOp",EDGE,"E9.3.0");var subQ2=makeQuery(id+"F12.imprint","INTERSECT",VERTEX,{"disambiguationData":[OD(1.0)],"derivedFrom":[subQ1,subQ0]});Q38=makeQuery(id+"F12.imprint","IMPRINT",FACE,{"disambiguationData":[TD([[makeQuery(id+"F12.imprint","IMPRINT",EDGE,{"disambiguationData":[TD([[subQ2,1.0]])],"derivedFrom":subQ0}),1.0]])]});}
            var Q39;
            {var subQ0=sQuery(id+"F12.wireOp",EDGE,"E9.5.0");var subQ1=sQuery(id+"F12.wireOp",EDGE,"E9.4.0");var subQ2=makeQuery(id+"F12.imprint","INTERSECT",VERTEX,{"disambiguationData":[OD(1.0)],"derivedFrom":[subQ1,subQ0]});Q39=makeQuery(id+"F12.imprint","IMPRINT",FACE,{"disambiguationData":[TD([[makeQuery(id+"F12.imprint","IMPRINT",EDGE,{"disambiguationData":[TD([[subQ2,1.0]])],"derivedFrom":subQ0}),1.0]])]});}
            var Q40;
            {var subQ0=sQuery(id+"F12.wireOp",EDGE,"E9.6.0");var subQ1=sQuery(id+"F12.wireOp",EDGE,"E9.5.0");var subQ2=makeQuery(id+"F12.imprint","INTERSECT",VERTEX,{"disambiguationData":[OD(1.0)],"derivedFrom":[subQ1,subQ0]});Q40=makeQuery(id+"F12.imprint","IMPRINT",FACE,{"disambiguationData":[TD([[makeQuery(id+"F12.imprint","IMPRINT",EDGE,{"disambiguationData":[TD([[subQ2,1.0]])],"derivedFrom":subQ0}),1.0]])]});}
            var Q41;
            {var subQ0=sQuery(id+"F12.wireOp",EDGE,"E9.7.0");var subQ1=sQuery(id+"F12.wireOp",EDGE,"E9.6.0");var subQ2=makeQuery(id+"F12.imprint","INTERSECT",VERTEX,{"disambiguationData":[OD(1.0)],"derivedFrom":[subQ1,subQ0]});Q41=makeQuery(id+"F12.imprint","IMPRINT",FACE,{"disambiguationData":[TD([[makeQuery(id+"F12.imprint","IMPRINT",EDGE,{"disambiguationData":[TD([[subQ2,1.0]])],"derivedFrom":subQ0}),1.0]])]});}
            var Q42;
            {var subQ0=sQuery(id+"F12.wireOp",EDGE,"E9.8.0");var subQ1=sQuery(id+"F12.wireOp",EDGE,"E9.7.0");var subQ2=makeQuery(id+"F12.imprint","INTERSECT",VERTEX,{"disambiguationData":[OD(1.0)],"derivedFrom":[subQ1,subQ0]});Q42=makeQuery(id+"F12.imprint","IMPRINT",FACE,{"disambiguationData":[TD([[makeQuery(id+"F12.imprint","IMPRINT",EDGE,{"disambiguationData":[TD([[subQ2,1.0]])],"derivedFrom":subQ0}),1.0]])]});}
            var Q43;
            {var subQ0=sQuery(id+"F12.wireOp",EDGE,"E9.9.0");var subQ1=sQuery(id+"F12.wireOp",EDGE,"E9.8.0");var subQ2=makeQuery(id+"F12.imprint","INTERSECT",VERTEX,{"disambiguationData":[OD(1.0)],"derivedFrom":[subQ1,subQ0]});Q43=makeQuery(id+"F12.imprint","IMPRINT",FACE,{"disambiguationData":[TD([[makeQuery(id+"F12.imprint","IMPRINT",EDGE,{"disambiguationData":[TD([[subQ2,1.0]])],"derivedFrom":subQ0}),1.0]])]});}
            var Q44;
            {var subQ0=sQuery(id+"F12.wireOp",EDGE,"E9.10.0");var subQ1=sQuery(id+"F12.wireOp",EDGE,"E9.9.0");var subQ2=makeQuery(id+"F12.imprint","INTERSECT",VERTEX,{"disambiguationData":[OD(1.0)],"derivedFrom":[subQ1,subQ0]});Q44=makeQuery(id+"F12.imprint","IMPRINT",FACE,{"disambiguationData":[TD([[makeQuery(id+"F12.imprint","IMPRINT",EDGE,{"disambiguationData":[TD([[subQ2,1.0]])],"derivedFrom":subQ0}),1.0]])]});}
            var Q45;
            {var subQ0=sQuery(id+"F12.wireOp",EDGE,"E9.11.0");var subQ1=sQuery(id+"F12.wireOp",EDGE,"E9.10.0");var subQ2=makeQuery(id+"F12.imprint","INTERSECT",VERTEX,{"disambiguationData":[OD(1.0)],"derivedFrom":[subQ1,subQ0]});Q45=makeQuery(id+"F12.imprint","IMPRINT",FACE,{"disambiguationData":[TD([[makeQuery(id+"F12.imprint","IMPRINT",EDGE,{"disambiguationData":[TD([[subQ2,1.0]])],"derivedFrom":subQ0}),1.0]])]});}
            var Q46;
            {var subQ0=sQuery(id+"F12.wireOp",EDGE,"E10.1.12.0");var subQ1=sQuery(id+"F12.wireOp",EDGE,"E9.11.0");var subQ2=makeQuery(id+"F12.imprint","INTERSECT",VERTEX,{"disambiguationData":[OD(1.0)],"derivedFrom":[subQ1,subQ0]});Q46=makeQuery(id+"F12.imprint","IMPRINT",FACE,{"disambiguationData":[TD([[makeQuery(id+"F12.imprint","IMPRINT",EDGE,{"disambiguationData":[TD([[subQ2,1.0]])],"derivedFrom":subQ0}),1.0]])]});}
            var Q47;
            {var subQ0=sQuery(id+"F12.wireOp",EDGE,"E10.1.13.0");var subQ1=sQuery(id+"F12.wireOp",EDGE,"E10.1.12.0");var subQ2=makeQuery(id+"F12.imprint","INTERSECT",VERTEX,{"disambiguationData":[OD(1.0)],"derivedFrom":[subQ1,subQ0]});Q47=makeQuery(id+"F12.imprint","IMPRINT",FACE,{"disambiguationData":[TD([[makeQuery(id+"F12.imprint","IMPRINT",EDGE,{"disambiguationData":[TD([[subQ2,1.0]])],"derivedFrom":subQ0}),1.0]])]});}
            var Q48;
            {var subQ0=sQuery(id+"F12.wireOp",EDGE,"E10.1.14.0");var subQ1=sQuery(id+"F12.wireOp",EDGE,"E10.1.13.0");var subQ2=makeQuery(id+"F12.imprint","INTERSECT",VERTEX,{"disambiguationData":[OD(1.0)],"derivedFrom":[subQ1,subQ0]});Q48=makeQuery(id+"F12.imprint","IMPRINT",FACE,{"disambiguationData":[TD([[makeQuery(id+"F12.imprint","IMPRINT",EDGE,{"disambiguationData":[TD([[subQ2,1.0]])],"derivedFrom":subQ0}),1.0]])]});}
            var Q49;
            {var subQ0=sQuery(id+"F12.wireOp",EDGE,"E10.1.15.0");var subQ1=sQuery(id+"F12.wireOp",EDGE,"E10.1.14.0");var subQ2=makeQuery(id+"F12.imprint","INTERSECT",VERTEX,{"disambiguationData":[OD(1.0)],"derivedFrom":[subQ1,subQ0]});Q49=makeQuery(id+"F12.imprint","IMPRINT",FACE,{"disambiguationData":[TD([[makeQuery(id+"F12.imprint","IMPRINT",EDGE,{"disambiguationData":[TD([[subQ2,1.0]])],"derivedFrom":subQ0}),1.0]])]});}
            var Q50;
            {var subQ0=sQuery(id+"F12.wireOp",EDGE,"E10.1.16.0");var subQ1=sQuery(id+"F12.wireOp",EDGE,"E10.1.15.0");var subQ2=makeQuery(id+"F12.imprint","INTERSECT",VERTEX,{"disambiguationData":[OD(1.0)],"derivedFrom":[subQ1,subQ0]});Q50=makeQuery(id+"F12.imprint","IMPRINT",FACE,{"disambiguationData":[TD([[makeQuery(id+"F12.imprint","IMPRINT",EDGE,{"disambiguationData":[TD([[subQ2,1.0]])],"derivedFrom":subQ0}),1.0]])]});}
            var Q51;
            {var subQ0=sQuery(id+"F12.wireOp",EDGE,"E10.1.17.0");var subQ1=sQuery(id+"F12.wireOp",EDGE,"E10.1.16.0");var subQ2=makeQuery(id+"F12.imprint","INTERSECT",VERTEX,{"disambiguationData":[OD(1.0)],"derivedFrom":[subQ1,subQ0]});Q51=makeQuery(id+"F12.imprint","IMPRINT",FACE,{"disambiguationData":[TD([[makeQuery(id+"F12.imprint","IMPRINT",EDGE,{"disambiguationData":[TD([[subQ2,1.0]])],"derivedFrom":subQ0}),1.0]])]});}
            var Q52;
            {var subQ0=sQuery(id+"F12.wireOp",EDGE,"E10.1.18.0");var subQ1=sQuery(id+"F12.wireOp",EDGE,"E10.1.17.0");var subQ2=makeQuery(id+"F12.imprint","INTERSECT",VERTEX,{"disambiguationData":[OD(1.0)],"derivedFrom":[subQ1,subQ0]});Q52=makeQuery(id+"F12.imprint","IMPRINT",FACE,{"disambiguationData":[TD([[makeQuery(id+"F12.imprint","IMPRINT",EDGE,{"disambiguationData":[TD([[subQ2,1.0]])],"derivedFrom":subQ0}),1.0]])]});}
            var Q53;
            {var subQ0=sQuery(id+"F12.wireOp",EDGE,"E10.1.19.0");var subQ1=sQuery(id+"F12.wireOp",EDGE,"E10.1.18.0");var subQ2=makeQuery(id+"F12.imprint","INTERSECT",VERTEX,{"disambiguationData":[OD(1.0)],"derivedFrom":[subQ1,subQ0]});Q53=makeQuery(id+"F12.imprint","IMPRINT",FACE,{"disambiguationData":[TD([[makeQuery(id+"F12.imprint","IMPRINT",EDGE,{"disambiguationData":[TD([[subQ2,1.0]])],"derivedFrom":subQ0}),1.0]])]});}
            var Q54;
            {var subQ0=sQuery(id+"F12.wireOp",EDGE,"E10.1.20.0");var subQ1=sQuery(id+"F12.wireOp",EDGE,"E10.1.19.0");var subQ2=makeQuery(id+"F12.imprint","INTERSECT",VERTEX,{"disambiguationData":[OD(1.0)],"derivedFrom":[subQ1,subQ0]});Q54=makeQuery(id+"F12.imprint","IMPRINT",FACE,{"disambiguationData":[TD([[makeQuery(id+"F12.imprint","IMPRINT",EDGE,{"disambiguationData":[TD([[subQ2,1.0]])],"derivedFrom":subQ0}),1.0]])]});}
            var Q55;
            {var subQ0=sQuery(id+"F12.wireOp",EDGE,"E10.1.21.0");var subQ1=sQuery(id+"F12.wireOp",EDGE,"E10.1.20.0");var subQ2=makeQuery(id+"F12.imprint","INTERSECT",VERTEX,{"disambiguationData":[OD(1.0)],"derivedFrom":[subQ1,subQ0]});Q55=makeQuery(id+"F12.imprint","IMPRINT",FACE,{"disambiguationData":[TD([[makeQuery(id+"F12.imprint","IMPRINT",EDGE,{"disambiguationData":[TD([[subQ2,1.0]])],"derivedFrom":subQ0}),1.0]])]});}
            var Q56;
            {var subQ0=sQuery(id+"F12.wireOp",EDGE,"E10.1.22.0");var subQ1=sQuery(id+"F12.wireOp",EDGE,"E10.1.21.0");var subQ2=makeQuery(id+"F12.imprint","INTERSECT",VERTEX,{"disambiguationData":[OD(1.0)],"derivedFrom":[subQ1,subQ0]});Q56=makeQuery(id+"F12.imprint","IMPRINT",FACE,{"disambiguationData":[TD([[makeQuery(id+"F12.imprint","IMPRINT",EDGE,{"disambiguationData":[TD([[subQ2,1.0]])],"derivedFrom":subQ1}),1.0]])]});}
            var Q57;
            {var subQ0=sQuery(id+"F12.wireOp",EDGE,"E10.1.23.0");var subQ1=sQuery(id+"F12.wireOp",EDGE,"E10.1.22.0");var subQ2=makeQuery(id+"F12.imprint","INTERSECT",VERTEX,{"disambiguationData":[OD(1.0)],"derivedFrom":[subQ1,subQ0]});Q57=makeQuery(id+"F12.imprint","IMPRINT",FACE,{"disambiguationData":[TD([[makeQuery(id+"F12.imprint","IMPRINT",EDGE,{"disambiguationData":[TD([[subQ2,1.0]])],"derivedFrom":subQ1}),1.0]])]});}
            var Q58;
            {var subQ0=sQuery(id+"F12.wireOp",EDGE,"E10.1.24.0");var subQ1=sQuery(id+"F12.wireOp",EDGE,"E10.1.23.0");var subQ2=makeQuery(id+"F12.imprint","INTERSECT",VERTEX,{"disambiguationData":[OD(1.0)],"derivedFrom":[subQ1,subQ0]});Q58=makeQuery(id+"F12.imprint","IMPRINT",FACE,{"disambiguationData":[TD([[makeQuery(id+"F12.imprint","IMPRINT",EDGE,{"disambiguationData":[TD([[subQ2,1.0]])],"derivedFrom":subQ0}),1.0]])]});}
            var Q59;
            {var subQ0=sQuery(id+"F12.wireOp",EDGE,"E10.1.25.0");var subQ1=sQuery(id+"F12.wireOp",EDGE,"E10.1.24.0");var subQ2=makeQuery(id+"F12.imprint","INTERSECT",VERTEX,{"disambiguationData":[OD(1.0)],"derivedFrom":[subQ1,subQ0]});Q59=makeQuery(id+"F12.imprint","IMPRINT",FACE,{"disambiguationData":[TD([[makeQuery(id+"F12.imprint","IMPRINT",EDGE,{"disambiguationData":[TD([[subQ2,1.0]])],"derivedFrom":subQ0}),1.0]])]});}
            var Q60;
            {var subQ0=sQuery(id+"F12.wireOp",EDGE,"E10.1.23.0");var subQ1=sQuery(id+"F12.wireOp",EDGE,"E10.1.22.0");var subQ2=makeQuery(id+"F12.imprint","INTERSECT",VERTEX,{"disambiguationData":[OD(1.0)],"derivedFrom":[subQ1,subQ0]});Q60=makeQuery(id+"F12.imprint","IMPRINT",FACE,{"disambiguationData":[TD([[makeQuery(id+"F12.imprint","IMPRINT",EDGE,{"disambiguationData":[TD([[subQ2,1.0]])],"derivedFrom":subQ0}),1.0]])]});}
            var Q61;
            {var subQ0=sQuery(id+"F12.wireOp",EDGE,"E10.1.22.0");var subQ1=sQuery(id+"F12.wireOp",EDGE,"E10.1.21.0");var subQ2=makeQuery(id+"F12.imprint","INTERSECT",VERTEX,{"disambiguationData":[OD(1.0)],"derivedFrom":[subQ1,subQ0]});Q61=makeQuery(id+"F12.imprint","IMPRINT",FACE,{"disambiguationData":[TD([[makeQuery(id+"F12.imprint","IMPRINT",EDGE,{"disambiguationData":[TD([[subQ2,1.0]])],"derivedFrom":subQ0}),1.0]])]});}
            var Q62;
            {var subQ0=sQuery(id+"F12.wireOp",EDGE,"E10.1.28.0");var subQ1=sQuery(id+"F12.wireOp",EDGE,"E10.1.27.0");var subQ2=makeQuery(id+"F12.imprint","INTERSECT",VERTEX,{"disambiguationData":[OD(1.0)],"derivedFrom":[subQ1,subQ0]});Q62=makeQuery(id+"F12.imprint","IMPRINT",FACE,{"disambiguationData":[TD([[makeQuery(id+"F12.imprint","IMPRINT",EDGE,{"disambiguationData":[TD([[subQ2,1.0]])],"derivedFrom":subQ0}),1.0]])]});}
            var Q63;
            {var subQ0=sQuery(id+"F12.wireOp",EDGE,"E10.1.29.0");var subQ1=sQuery(id+"F12.wireOp",EDGE,"E10.1.28.0");var subQ2=makeQuery(id+"F12.imprint","INTERSECT",VERTEX,{"disambiguationData":[OD(1.0)],"derivedFrom":[subQ1,subQ0]});Q63=makeQuery(id+"F12.imprint","IMPRINT",FACE,{"disambiguationData":[TD([[makeQuery(id+"F12.imprint","IMPRINT",EDGE,{"disambiguationData":[TD([[subQ2,1.0]])],"derivedFrom":subQ1}),1.0]])]});}
            var Q64;
            {var subQ0=sQuery(id+"F12.wireOp",EDGE,"E10.1.29.0");var subQ1=sQuery(id+"F12.wireOp",EDGE,"E10.1.28.0");var subQ2=makeQuery(id+"F12.imprint","INTERSECT",VERTEX,{"disambiguationData":[OD(1.0)],"derivedFrom":[subQ1,subQ0]});Q64=makeQuery(id+"F12.imprint","IMPRINT",FACE,{"disambiguationData":[TD([[makeQuery(id+"F12.imprint","IMPRINT",EDGE,{"disambiguationData":[TD([[subQ2,1.0]])],"derivedFrom":subQ0}),1.0]])]});}
            var Q65;
            {var subQ0=sQuery(id+"F12.wireOp",EDGE,"E10.1.30.0");var subQ1=sQuery(id+"F12.wireOp",EDGE,"E10.1.29.0");var subQ2=makeQuery(id+"F12.imprint","INTERSECT",VERTEX,{"disambiguationData":[OD(1.0)],"derivedFrom":[subQ1,subQ0]});Q65=makeQuery(id+"F12.imprint","IMPRINT",FACE,{"disambiguationData":[TD([[makeQuery(id+"F12.imprint","IMPRINT",EDGE,{"disambiguationData":[TD([[subQ2,1.0]])],"derivedFrom":subQ1}),1.0]])]});}
            var Q66;
            {var subQ0=sQuery(id+"F12.wireOp",EDGE,"E10.1.30.0");var subQ1=sQuery(id+"F12.wireOp",EDGE,"E10.1.29.0");var subQ2=makeQuery(id+"F12.imprint","INTERSECT",VERTEX,{"disambiguationData":[OD(1.0)],"derivedFrom":[subQ1,subQ0]});Q66=makeQuery(id+"F12.imprint","IMPRINT",FACE,{"disambiguationData":[TD([[makeQuery(id+"F12.imprint","IMPRINT",EDGE,{"disambiguationData":[TD([[subQ2,1.0]])],"derivedFrom":subQ0}),1.0]])]});}
            var Q67;
            {var subQ0=sQuery(id+"F12.wireOp",EDGE,"E10.1.31.0");var subQ1=sQuery(id+"F12.wireOp",EDGE,"E10.1.30.0");var subQ2=makeQuery(id+"F12.imprint","INTERSECT",VERTEX,{"disambiguationData":[OD(1.0)],"derivedFrom":[subQ1,subQ0]});Q67=makeQuery(id+"F12.imprint","IMPRINT",FACE,{"disambiguationData":[TD([[makeQuery(id+"F12.imprint","IMPRINT",EDGE,{"disambiguationData":[TD([[subQ2,1.0]])],"derivedFrom":subQ1}),1.0]])]});}
            var Q68;
            {var subQ0=sQuery(id+"F12.wireOp",EDGE,"E10.1.31.0");var subQ1=sQuery(id+"F12.wireOp",EDGE,"E10.1.30.0");var subQ2=makeQuery(id+"F12.imprint","INTERSECT",VERTEX,{"disambiguationData":[OD(1.0)],"derivedFrom":[subQ1,subQ0]});Q68=makeQuery(id+"F12.imprint","IMPRINT",FACE,{"disambiguationData":[TD([[makeQuery(id+"F12.imprint","IMPRINT",EDGE,{"disambiguationData":[TD([[subQ2,1.0]])],"derivedFrom":subQ0}),1.0]])]});}
            var Q69;
            {var subQ0=sQuery(id+"F12.wireOp",EDGE,"E10.1.32.0");var subQ1=sQuery(id+"F12.wireOp",EDGE,"E10.1.31.0");var subQ2=makeQuery(id+"F12.imprint","INTERSECT",VERTEX,{"disambiguationData":[OD(1.0)],"derivedFrom":[subQ1,subQ0]});Q69=makeQuery(id+"F12.imprint","IMPRINT",FACE,{"disambiguationData":[TD([[makeQuery(id+"F12.imprint","IMPRINT",EDGE,{"disambiguationData":[TD([[subQ2,1.0]])],"derivedFrom":subQ0}),1.0]])]});}
            var Q70;
            {var subQ0=sQuery(id+"F12.wireOp",EDGE,"E10.1.27.0");var subQ1=sQuery(id+"F12.wireOp",EDGE,"E10.1.26.0");var subQ2=makeQuery(id+"F12.imprint","INTERSECT",VERTEX,{"disambiguationData":[OD(1.0)],"derivedFrom":[subQ1,subQ0]});Q70=makeQuery(id+"F12.imprint","IMPRINT",FACE,{"disambiguationData":[TD([[makeQuery(id+"F12.imprint","IMPRINT",EDGE,{"disambiguationData":[TD([[subQ2,1.0]])],"derivedFrom":subQ0}),1.0]])]});}
            var Q71;
            {var subQ0=sQuery(id+"F12.wireOp",EDGE,"E10.1.26.0");var subQ1=sQuery(id+"F12.wireOp",EDGE,"E10.1.25.0");var subQ2=makeQuery(id+"F12.imprint","INTERSECT",VERTEX,{"disambiguationData":[OD(1.0)],"derivedFrom":[subQ1,subQ0]});Q71=makeQuery(id+"F12.imprint","IMPRINT",FACE,{"disambiguationData":[TD([[makeQuery(id+"F12.imprint","IMPRINT",EDGE,{"disambiguationData":[TD([[subQ2,1.0]])],"derivedFrom":subQ0}),1.0]])]});}
            var Q72;
            {var subQ0=sQuery(id+"F12.wireOp",EDGE,"E11.1.33.0");var subQ1=sQuery(id+"F12.wireOp",EDGE,"E10.1.32.0");var subQ2=makeQuery(id+"F12.imprint","INTERSECT",VERTEX,{"disambiguationData":[OD(1.0)],"derivedFrom":[subQ1,subQ0]});Q72=makeQuery(id+"F12.imprint","IMPRINT",FACE,{"disambiguationData":[TD([[makeQuery(id+"F12.imprint","IMPRINT",EDGE,{"disambiguationData":[TD([[subQ2,1.0]])],"derivedFrom":subQ0}),1.0]])]});}
            var Q73;
            {var subQ0=sQuery(id+"F12.wireOp",EDGE,"E10.1.32.0");var subQ1=sQuery(id+"F12.wireOp",EDGE,"E10.1.31.0");var subQ2=makeQuery(id+"F12.imprint","INTERSECT",VERTEX,{"disambiguationData":[OD(0.0)],"derivedFrom":[subQ1,subQ0]});Q73=makeQuery(id+"F12.imprint","IMPRINT",FACE,{"disambiguationData":[TD([[makeQuery(id+"F12.imprint","IMPRINT",EDGE,{"disambiguationData":[TD([[subQ2,-1.0]])],"derivedFrom":subQ1}),1.0]])]});}
            var Q74;
            {var subQ0=sQuery(id+"F12.wireOp",EDGE,"E11.1.33.0");var subQ1=sQuery(id+"F12.wireOp",EDGE,"E10.1.32.0");var subQ2=makeQuery(id+"F12.imprint","INTERSECT",VERTEX,{"disambiguationData":[OD(0.0)],"derivedFrom":[subQ1,subQ0]});Q74=makeQuery(id+"F12.imprint","IMPRINT",FACE,{"disambiguationData":[TD([[makeQuery(id+"F12.imprint","IMPRINT",EDGE,{"disambiguationData":[TD([[subQ2,-1.0]])],"derivedFrom":subQ1}),1.0]])]});}
            var Q75;
            {var subQ0=sQuery(id+"F12.wireOp",EDGE,"E10.1.21.0");var subQ1=sQuery(id+"F12.wireOp",EDGE,"E10.1.20.0");var subQ2=makeQuery(id+"F12.imprint","INTERSECT",VERTEX,{"disambiguationData":[OD(1.0)],"derivedFrom":[subQ1,subQ0]});Q75=makeQuery(id+"F12.imprint","IMPRINT",FACE,{"disambiguationData":[TD([[makeQuery(id+"F12.imprint","IMPRINT",EDGE,{"disambiguationData":[TD([[subQ2,1.0]])],"derivedFrom":subQ1}),1.0]])]});}
            var Q76;
            {var subQ0=sQuery(id+"F12.wireOp",EDGE,"E10.1.20.0");var subQ1=sQuery(id+"F12.wireOp",EDGE,"E10.1.19.0");var subQ2=makeQuery(id+"F12.imprint","INTERSECT",VERTEX,{"disambiguationData":[OD(1.0)],"derivedFrom":[subQ1,subQ0]});Q76=makeQuery(id+"F12.imprint","IMPRINT",FACE,{"disambiguationData":[TD([[makeQuery(id+"F12.imprint","IMPRINT",EDGE,{"disambiguationData":[TD([[subQ2,1.0]])],"derivedFrom":subQ1}),1.0]])]});}
            var Q77;
            {var subQ0=sQuery(id+"F12.wireOp",EDGE,"E10.1.19.0");var subQ1=sQuery(id+"F12.wireOp",EDGE,"E10.1.18.0");var subQ2=makeQuery(id+"F12.imprint","INTERSECT",VERTEX,{"disambiguationData":[OD(1.0)],"derivedFrom":[subQ1,subQ0]});Q77=makeQuery(id+"F12.imprint","IMPRINT",FACE,{"disambiguationData":[TD([[makeQuery(id+"F12.imprint","IMPRINT",EDGE,{"disambiguationData":[TD([[subQ2,1.0]])],"derivedFrom":subQ1}),1.0]])]});}
            var Q78;
            {var subQ0=sQuery(id+"F12.wireOp",EDGE,"E10.1.18.0");var subQ1=sQuery(id+"F12.wireOp",EDGE,"E10.1.17.0");var subQ2=makeQuery(id+"F12.imprint","INTERSECT",VERTEX,{"disambiguationData":[OD(1.0)],"derivedFrom":[subQ1,subQ0]});Q78=makeQuery(id+"F12.imprint","IMPRINT",FACE,{"disambiguationData":[TD([[makeQuery(id+"F12.imprint","IMPRINT",EDGE,{"disambiguationData":[TD([[subQ2,1.0]])],"derivedFrom":subQ1}),1.0]])]});}
            var Q79;
            {var subQ0=sQuery(id+"F12.wireOp",EDGE,"E10.1.17.0");var subQ1=sQuery(id+"F12.wireOp",EDGE,"E10.1.16.0");var subQ2=makeQuery(id+"F12.imprint","INTERSECT",VERTEX,{"disambiguationData":[OD(1.0)],"derivedFrom":[subQ1,subQ0]});Q79=makeQuery(id+"F12.imprint","IMPRINT",FACE,{"disambiguationData":[TD([[makeQuery(id+"F12.imprint","IMPRINT",EDGE,{"disambiguationData":[TD([[subQ2,1.0]])],"derivedFrom":subQ1}),1.0]])]});}
            var Q80;
            {var subQ0=sQuery(id+"F12.wireOp",EDGE,"E10.1.16.0");var subQ1=sQuery(id+"F12.wireOp",EDGE,"E10.1.15.0");var subQ2=makeQuery(id+"F12.imprint","INTERSECT",VERTEX,{"disambiguationData":[OD(1.0)],"derivedFrom":[subQ1,subQ0]});Q80=makeQuery(id+"F12.imprint","IMPRINT",FACE,{"disambiguationData":[TD([[makeQuery(id+"F12.imprint","IMPRINT",EDGE,{"disambiguationData":[TD([[subQ2,1.0]])],"derivedFrom":subQ1}),1.0]])]});}
            var Q81;
            {var subQ0=sQuery(id+"F12.wireOp",EDGE,"E10.1.15.0");var subQ1=sQuery(id+"F12.wireOp",EDGE,"E10.1.14.0");var subQ2=makeQuery(id+"F12.imprint","INTERSECT",VERTEX,{"disambiguationData":[OD(1.0)],"derivedFrom":[subQ1,subQ0]});Q81=makeQuery(id+"F12.imprint","IMPRINT",FACE,{"disambiguationData":[TD([[makeQuery(id+"F12.imprint","IMPRINT",EDGE,{"disambiguationData":[TD([[subQ2,1.0]])],"derivedFrom":subQ1}),1.0]])]});}
            var Q82;
            {var subQ0=sQuery(id+"F12.wireOp",EDGE,"E11.1.33.0");var subQ1=sQuery(id+"F12.wireOp",EDGE,"E10.1.32.0");var subQ2=makeQuery(id+"F12.imprint","INTERSECT",VERTEX,{"disambiguationData":[OD(1.0)],"derivedFrom":[subQ1,subQ0]});Q82=makeQuery(id+"F12.imprint","IMPRINT",FACE,{"disambiguationData":[TD([[makeQuery(id+"F12.imprint","IMPRINT",EDGE,{"disambiguationData":[TD([[subQ2,1.0]])],"derivedFrom":subQ1}),1.0]])]});}
            var Q83;
            {var subQ0=sQuery(id+"F12.wireOp",EDGE,"E10.1.32.0");var subQ1=sQuery(id+"F12.wireOp",EDGE,"E10.1.31.0");var subQ2=makeQuery(id+"F12.imprint","INTERSECT",VERTEX,{"disambiguationData":[OD(1.0)],"derivedFrom":[subQ1,subQ0]});Q83=makeQuery(id+"F12.imprint","IMPRINT",FACE,{"disambiguationData":[TD([[makeQuery(id+"F12.imprint","IMPRINT",EDGE,{"disambiguationData":[TD([[subQ2,1.0]])],"derivedFrom":subQ1}),1.0]])]});}
            var Q84;
            {var subQ0=sQuery(id+"F12.wireOp",EDGE,"E10.1.28.0");var subQ1=sQuery(id+"F12.wireOp",EDGE,"E10.1.27.0");var subQ2=makeQuery(id+"F12.imprint","INTERSECT",VERTEX,{"disambiguationData":[OD(1.0)],"derivedFrom":[subQ1,subQ0]});Q84=makeQuery(id+"F12.imprint","IMPRINT",FACE,{"disambiguationData":[TD([[makeQuery(id+"F12.imprint","IMPRINT",EDGE,{"disambiguationData":[TD([[subQ2,1.0]])],"derivedFrom":subQ1}),1.0]])]});}
            var Q85;
            {var subQ0=sQuery(id+"F12.wireOp",EDGE,"E10.1.27.0");var subQ1=sQuery(id+"F12.wireOp",EDGE,"E10.1.26.0");var subQ2=makeQuery(id+"F12.imprint","INTERSECT",VERTEX,{"disambiguationData":[OD(1.0)],"derivedFrom":[subQ1,subQ0]});Q85=makeQuery(id+"F12.imprint","IMPRINT",FACE,{"disambiguationData":[TD([[makeQuery(id+"F12.imprint","IMPRINT",EDGE,{"disambiguationData":[TD([[subQ2,1.0]])],"derivedFrom":subQ1}),1.0]])]});}
            var Q86;
            {var subQ0=sQuery(id+"F12.wireOp",EDGE,"E10.1.26.0");var subQ1=sQuery(id+"F12.wireOp",EDGE,"E10.1.25.0");var subQ2=makeQuery(id+"F12.imprint","INTERSECT",VERTEX,{"disambiguationData":[OD(1.0)],"derivedFrom":[subQ1,subQ0]});Q86=makeQuery(id+"F12.imprint","IMPRINT",FACE,{"disambiguationData":[TD([[makeQuery(id+"F12.imprint","IMPRINT",EDGE,{"disambiguationData":[TD([[subQ2,1.0]])],"derivedFrom":subQ1}),1.0]])]});}
            var Q87;
            {var subQ0=sQuery(id+"F12.wireOp",EDGE,"E10.1.25.0");var subQ1=sQuery(id+"F12.wireOp",EDGE,"E10.1.24.0");var subQ2=makeQuery(id+"F12.imprint","INTERSECT",VERTEX,{"disambiguationData":[OD(1.0)],"derivedFrom":[subQ1,subQ0]});Q87=makeQuery(id+"F12.imprint","IMPRINT",FACE,{"disambiguationData":[TD([[makeQuery(id+"F12.imprint","IMPRINT",EDGE,{"disambiguationData":[TD([[subQ2,1.0]])],"derivedFrom":subQ1}),1.0]])]});}
            var Q88;
            {var subQ0=sQuery(id+"F12.wireOp",EDGE,"E10.1.24.0");var subQ1=sQuery(id+"F12.wireOp",EDGE,"E10.1.23.0");var subQ2=makeQuery(id+"F12.imprint","INTERSECT",VERTEX,{"disambiguationData":[OD(1.0)],"derivedFrom":[subQ1,subQ0]});Q88=makeQuery(id+"F12.imprint","IMPRINT",FACE,{"disambiguationData":[TD([[makeQuery(id+"F12.imprint","IMPRINT",EDGE,{"disambiguationData":[TD([[subQ2,1.0]])],"derivedFrom":subQ1}),1.0]])]});}
            extrude(context, id + "F13", {"entities" : qUnion([Q0, Q1, Q2, Q3, Q4, Q5, Q6, Q7, Q8, Q9, Q10, Q11, Q12, Q13, Q14, Q15, Q16, Q17, Q18, Q19, Q20, Q21, Q22, Q23, Q24, Q25, Q26, Q27, Q28, Q29, Q30, Q31, Q32, Q33, Q34, Q35, Q36, Q37, Q38, Q39, Q40, Q41, Q42, Q43, Q44, Q45, Q46, Q47, Q48, Q49, Q50, Q51, Q52, Q53, Q54, Q55, Q56, Q57, Q58, Q59, Q60, Q61, Q62, Q63, Q64, Q65, Q66, Q67, Q68, Q69, Q70, Q71, Q72, Q73, Q74, Q75, Q76, Q77, Q78, Q79, Q80, Q81, Q82, Q83, Q84, Q85, Q86, Q87, Q88]), "operationType" : NewBodyOperationType.REMOVE, "oppositeDirection" : true, "depth" : 25 * mm, "offsetDistance" : 25 * mm});
        }
        {
            var Q0;
            Q0=qCreatedBy(makeId("Front.planeOp"),FACE);
            var sketch = newSketch(context, id + "F14", { "sketchPlane" : qUnion([Q0])});
            skLineSegment(sketch, "E13.bottom", {"start": v(-13, 40) * mm, "end": v(-5, 40) * mm});
            skLineSegment(sketch, "E13.top", {"start": v(-13, 35) * mm, "end": v(-5, 35) * mm});
            skLineSegment(sketch, "E13.left", {"start": v(-13, 40) * mm, "end": v(-13, 35) * mm});
            skLineSegment(sketch, "E13.right", {"start": v(-5, 40) * mm, "end": v(-5, 35) * mm});
            skSolve(sketch);
        }
        {
            var Q0;
            Q0=makeQuery(id+"F14.imprint","IMPRINT",FACE,{"disambiguationData":[TD([[makeQuery(id+"F14.imprint","IMPRINT",EDGE,{"derivedFrom":sQuery(id+"F14.wireOp",EDGE,"E13.bottom")}),-1.0]])]});
            var Q1;
            Q1=makeQuery(id+"F1.opExtrude","SWEPT_FACE",FACE,{"disambiguationData":[OSD([sQuery(id+"F0.wireOp",EDGE,"E0")])]});
            revolve(context, id + "F15", {"surfaceOperationType" : NewSurfaceOperationType.NEW, "entities" : qUnion([Q0]), "axis" : qUnion([Q1]), "revolveType" : RevolveType.FULL});
        }
        {
            var Q0;
            Q0=makeQuery(id+"F11.opRevolve","SWEPT_BODY",BODY,{"disambiguationData":[OSD([sQuery(id+"F10.wireOp",EDGE,"E7.bottom"),sQuery(id+"F10.wireOp",EDGE,"E7.top"),sQuery(id+"F10.wireOp",EDGE,"E7.left"),sQuery(id+"F10.wireOp",EDGE,"E7.right")])]});
            transform(context, id + "F16", {"entities" : qUnion([Q0]), "transformType" : TransformType.TRANSLATION_3D, "dx" : 0 * mm, "dy" : 0 * mm, "dz" : 0 * mm, "makeCopy" : true});
        }
    });
